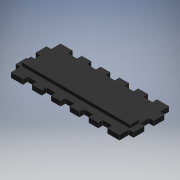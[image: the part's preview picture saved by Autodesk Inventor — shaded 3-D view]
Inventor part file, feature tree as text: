
AUTODESK INVENTOR PART (.ipt)
format: ipt  version: 2019 (Build 230136000, 136)  size: 206,336 bytes
history: native  units: mm
features: extrude x3, sketch x3, projected_geometry x1
ambient origin geometry x8: Origin, YZ Plane, XZ Plane, XY Plane, X Axis, Y Axis, Z Axis, Center Point
bodies: Solid1 (feature_tree)
feature tree (7):
  extrude  "Extrusion1"  Depth=42.0mm
  extrude  "Extrusion2"  Depth=4.0mm
  extrude  "Extrusion3"  Depth=8.0mm
  sketch  "Sketch1"  dims[d0=100.0mm d1=42.0mm]
  sketch  "Sketch2"  dims[d2=4.0mm d3=0.0mm d4=4.0mm]
  projected_geometry  "Projected Loop1"
  sketch  "Sketch3"  dims[d5=4.0mm d7=8.0mm d8=8.0mm d10=8.0mm d11=8.0mm d13=4.0mm d14=8.0mm d15=4.0mm d16=0.0mm d17=5.0mm d18=8.0mm d19=3.0mm d20=0.0mm]
